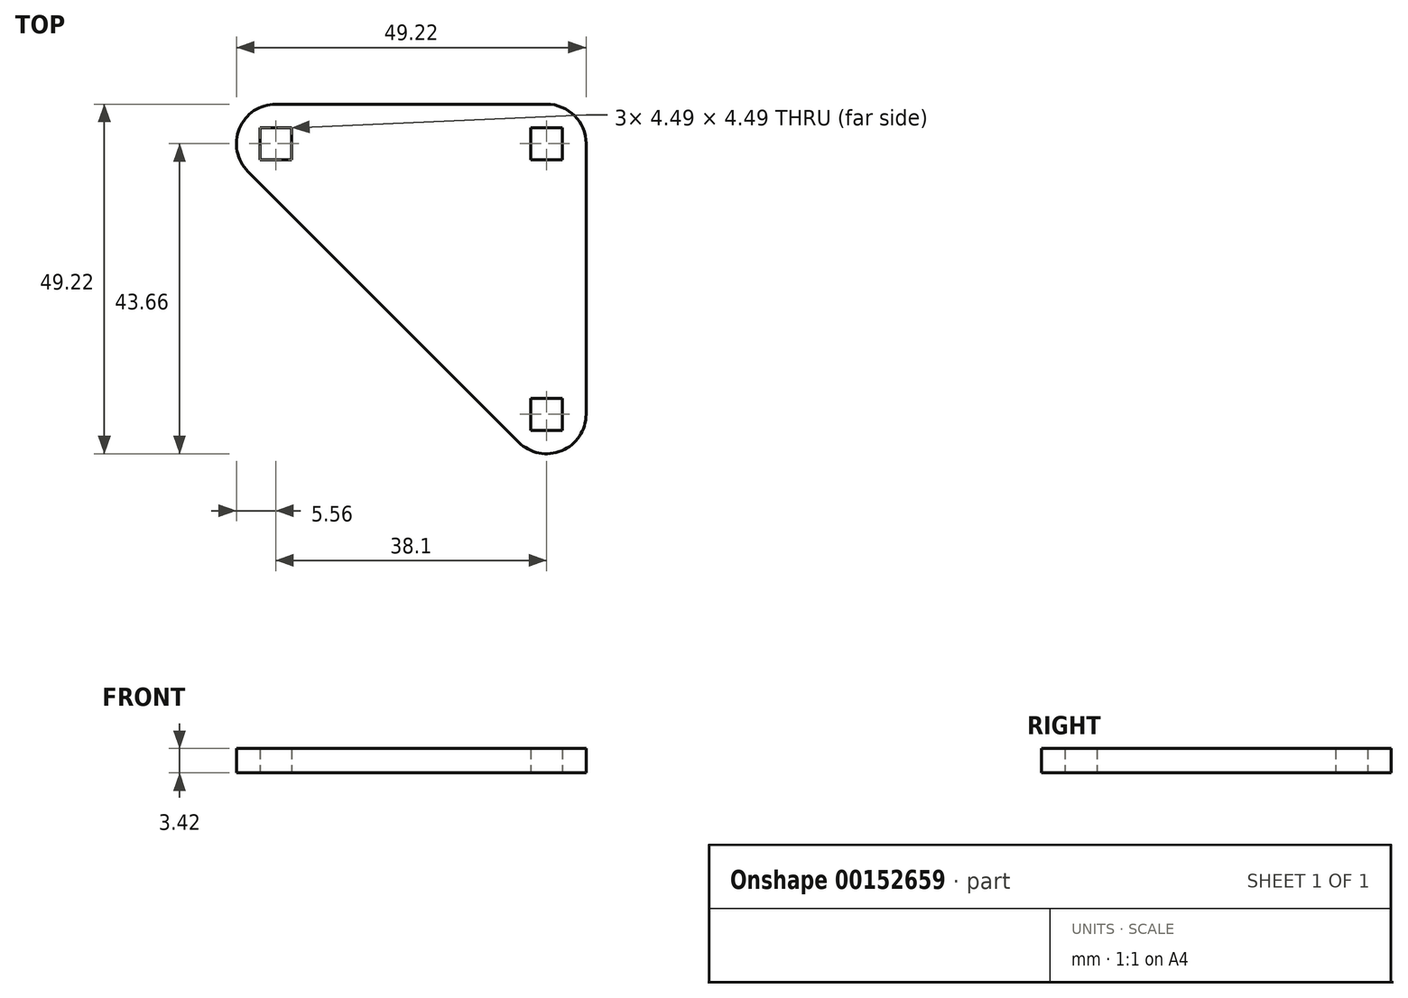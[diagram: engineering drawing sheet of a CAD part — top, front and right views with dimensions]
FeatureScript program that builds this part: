
annotation { "Feature Type Name" : "Feature", "Feature Type Description" : "" }
export const myFeature = defineFeature(function(context is Context, id is Id, definition is map)
    precondition{}
    {
        {
            var Q0;
            Q0=qCreatedBy(makeId("Top.planeOp"),FACE);
            var sketch = newSketch(context, id + "F0", { "sketchPlane" : qUnion([Q0])});
            skLineSegment(sketch, "E0", {"start": v(0, 0) * mm, "end": v(0, 38.1) * mm, "construction": true});
            skLineSegment(sketch, "E1", {"start": v(0, 0) * mm, "end": v(-38.1, 38.1) * mm, "construction": true});
            skLineSegment(sketch, "E2", {"start": v(-38.1, 38.1) * mm, "end": v(0, 38.1) * mm, "construction": true});
            skLineSegment(sketch, "E3.bottom", {"start": v(2.25, -2.25) * mm, "end": v(-2.25, -2.25) * mm});
            skLineSegment(sketch, "E3.top", {"start": v(2.25, 2.25) * mm, "end": v(-2.25, 2.25) * mm});
            skLineSegment(sketch, "E3.left", {"start": v(2.25, -2.25) * mm, "end": v(2.25, 2.25) * mm});
            skLineSegment(sketch, "E3.right", {"start": v(-2.25, -2.25) * mm, "end": v(-2.25, 2.25) * mm});
            skPoint(sketch, "E3.middle", {"position": v(0, 0) * mm});
            skLineSegment(sketch, "E4.bottom", {"start": v(2.25, 35.85) * mm, "end": v(-2.25, 35.85) * mm});
            skLineSegment(sketch, "E4.top", {"start": v(2.25, 40.35) * mm, "end": v(-2.25, 40.35) * mm});
            skLineSegment(sketch, "E4.left", {"start": v(2.25, 35.85) * mm, "end": v(2.25, 40.35) * mm});
            skLineSegment(sketch, "E4.right", {"start": v(-2.25, 35.85) * mm, "end": v(-2.25, 40.35) * mm});
            skPoint(sketch, "E4.middle", {"position": v(0, 38.1) * mm});
            skLineSegment(sketch, "E5.bottom", {"start": v(-35.85, 35.85) * mm, "end": v(-40.35, 35.85) * mm});
            skLineSegment(sketch, "E5.top", {"start": v(-35.85, 40.35) * mm, "end": v(-40.35, 40.35) * mm});
            skLineSegment(sketch, "E5.left", {"start": v(-35.85, 35.85) * mm, "end": v(-35.85, 40.35) * mm});
            skLineSegment(sketch, "E5.right", {"start": v(-40.35, 35.85) * mm, "end": v(-40.35, 40.35) * mm});
            skPoint(sketch, "E5.middle", {"position": v(-38.1, 38.1) * mm});
            skCircle(sketch, "E6", {"center": v(0, 38.1) * mm, "radius": 3.18 * mm, "construction": true});
            skArc(sketch, "E7", {"start": v(5.56, 38.1) * mm, "mid": v(3.93, 42.03) * mm, "end": v(0, 43.66) * mm});
            skArc(sketch, "E8", {"start": v(-38.1, 43.66) * mm, "mid": v(-43.23, 40.23) * mm, "end": v(-42.03, 34.17) * mm});
            skArc(sketch, "E9", {"start": v(-3.93, -3.93) * mm, "mid": v(2.13, -5.13) * mm, "end": v(5.56, 0) * mm});
            skLineSegment(sketch, "E10", {"start": v(-42.03, 34.17) * mm, "end": v(-3.93, -3.93) * mm});
            skLineSegment(sketch, "E11", {"start": v(5.56, 0) * mm, "end": v(5.56, 38.1) * mm});
            skLineSegment(sketch, "E12", {"start": v(-38.1, 43.66) * mm, "end": v(0, 43.66) * mm});
            skSolve(sketch);
        }
        {
            var Q0;
            Q0 = qSketchRegion(id + "F0", true);
            extrude(context, id + "F1", {"entities" : qUnion([Q0]), "depth" : 3.42 * mm});
        }
    });
